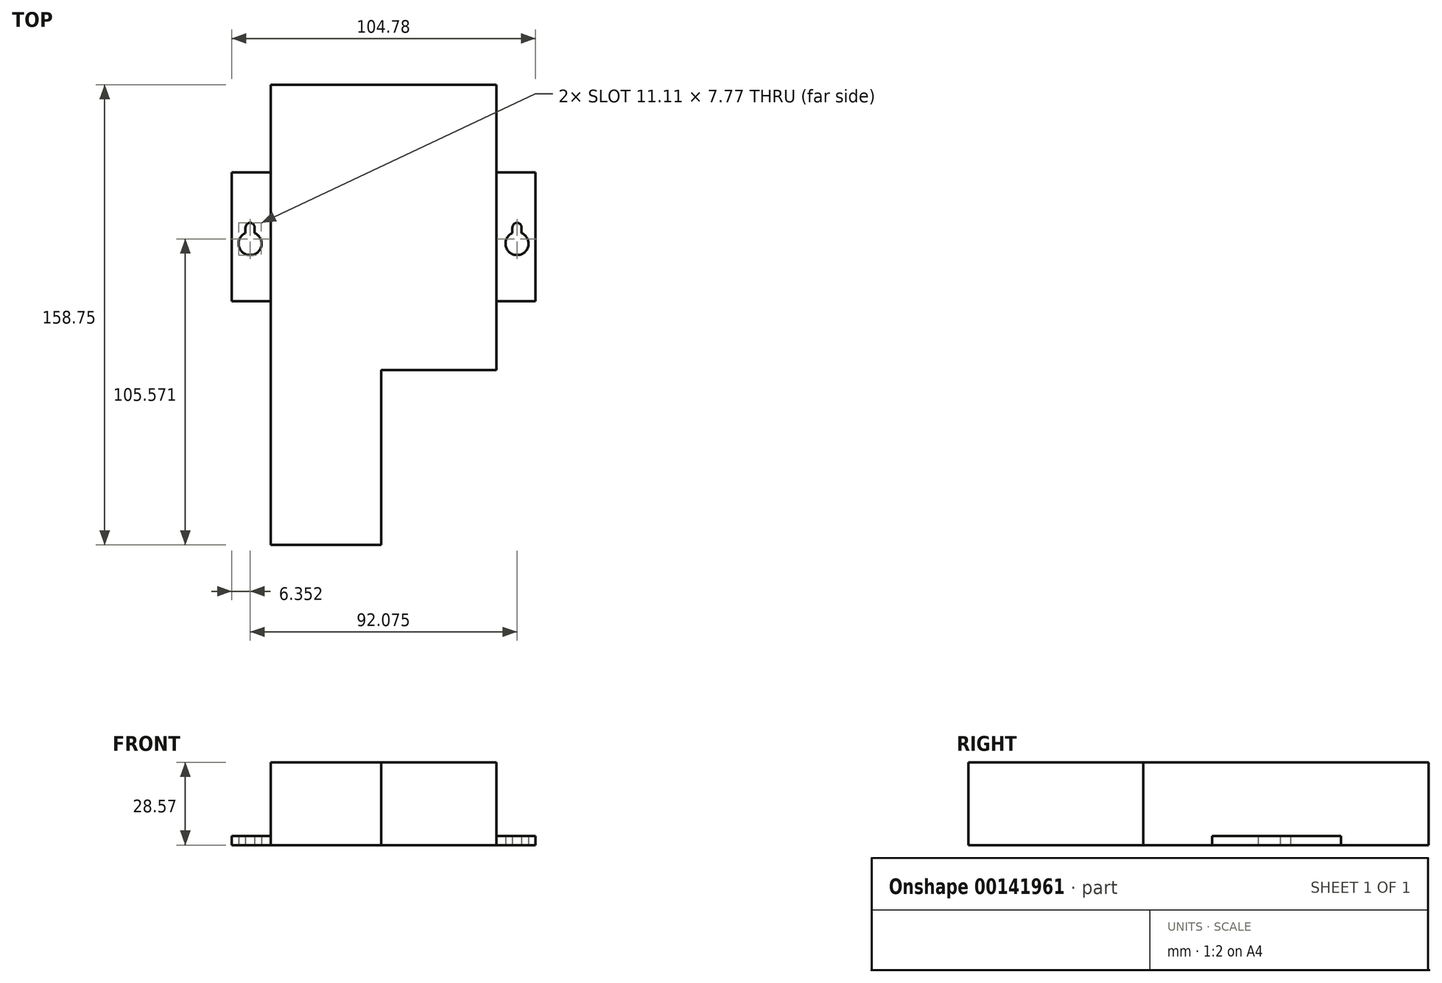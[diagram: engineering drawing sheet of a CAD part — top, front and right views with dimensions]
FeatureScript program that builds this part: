
annotation { "Feature Type Name" : "Feature", "Feature Type Description" : "" }
export const myFeature = defineFeature(function(context is Context, id is Id, definition is map)
    precondition{}
    {
        {
            var Q0;
            Q0=qCreatedBy(makeId("Top.planeOp"),FACE);
            var sketch = newSketch(context, id + "F0", { "sketchPlane" : qUnion([Q0])});
            skLineSegment(sketch, "E0.bottom", {"start": v(-38.9, -49.21) * mm, "end": v(38.9, -49.21) * mm});
            skLineSegment(sketch, "E0.top", {"start": v(-38.9, 49.21) * mm, "end": v(38.9, 49.21) * mm});
            skLineSegment(sketch, "E0.left", {"start": v(-38.9, -49.21) * mm, "end": v(-38.9, 49.21) * mm});
            skLineSegment(sketch, "E0.right", {"start": v(38.9, -49.21) * mm, "end": v(38.9, 49.21) * mm});
            skPoint(sketch, "E0.middle", {"position": v(0, 0) * mm});
            skSolve(sketch);
        }
        {
            var Q0;
            Q0 = qSketchRegion(id + "F0", true);
            extrude(context, id + "F1", {"entities" : qUnion([Q0]), "depth" : 28.57 * mm});
        }
        {
            var Q0;
            Q0=makeQuery(id+"F1.opExtrude","CAP_FACE",FACE,{"disambiguationData":[OSD([sQuery(id+"F0.wireOp",EDGE,"E0.bottom"),sQuery(id+"F0.wireOp",EDGE,"E0.top"),sQuery(id+"F0.wireOp",EDGE,"E0.left"),sQuery(id+"F0.wireOp",EDGE,"E0.right")])],"isStart":true});
            var sketch = newSketch(context, id + "F2", { "sketchPlane" : qUnion([Q0])});
            skPoint(sketch, "E1.middle", {"position": v(0, 0) * mm});
            skCircle(sketch, "E2", {"center": v(-46.04, 5.56) * mm, "radius": 3.97 * mm});
            skLineSegment(sketch, "E3", {"start": v(-46.04, 5.56) * mm, "end": v(-46.04, 0) * mm, "construction": true});
            skArc(sketch, "E4.0.startCap", {"start": v(-47.63, 5.56) * mm, "mid": v(-46.04, 7.14) * mm, "end": v(-44.45, 5.56) * mm});
            skArc(sketch, "E4.0.endCap", {"start": v(-44.45, 0) * mm, "mid": v(-46.04, -1.59) * mm, "end": v(-47.63, 0) * mm});
            skLineSegment(sketch, "E4.0.left", {"start": v(-44.45, 5.56) * mm, "end": v(-44.45, 0) * mm});
            skLineSegment(sketch, "E4.0.right", {"start": v(-47.63, 5.56) * mm, "end": v(-47.63, 0) * mm});
            skLineSegment(sketch, "E5", {"start": v(0, 0) * mm, "end": v(0, -42.43) * mm, "construction": true});
            skLineSegment(sketch, "E6.MirrorCS", {"start": v(46.04, 5.56) * mm, "end": v(46.04, 0) * mm, "construction": true});
            skCircle(sketch, "E7.MirrorC", {"center": v(46.04, 5.56) * mm, "radius": 3.97 * mm});
            skArc(sketch, "E8.MirrorCS", {"start": v(47.63, 5.56) * mm, "mid": v(46.04, 7.14) * mm, "end": v(44.45, 5.56) * mm});
            skArc(sketch, "E9.MirrorCS", {"start": v(44.45, 0) * mm, "mid": v(46.04, -1.59) * mm, "end": v(47.63, 0) * mm});
            skLineSegment(sketch, "E10.MirrorCS", {"start": v(44.45, 5.56) * mm, "end": v(44.45, 0) * mm});
            skLineSegment(sketch, "E11.MirrorCS", {"start": v(47.62, 5.56) * mm, "end": v(47.62, 0) * mm});
            skLineSegment(sketch, "E12.bottom", {"start": v(-52.39, 25.4) * mm, "end": v(52.39, 25.4) * mm});
            skLineSegment(sketch, "E12.top", {"start": v(-52.39, -19.05) * mm, "end": v(52.39, -19.05) * mm});
            skLineSegment(sketch, "E12.left", {"start": v(-52.39, 25.4) * mm, "end": v(-52.39, -19.05) * mm});
            skLineSegment(sketch, "E12.right", {"start": v(52.39, 25.4) * mm, "end": v(52.39, -19.05) * mm});
            skLineSegment(sketch, "E13", {"start": v(0, 49.21) * mm, "end": v(0, 25.4) * mm, "construction": true});
            skSolve(sketch);
        }
        {
            var Q0;
            Q0 = qSketchRegion(id + "F2", true);
            extrude(context, id + "F3", {"entities" : qUnion([Q0]), "operationType" : NewBodyOperationType.ADD, "oppositeDirection" : true, "depth" : 3.17 * mm});
        }
        {
            var Q0;
            Q0=makeQuery(id+"F1.opExtrude","SWEPT_FACE",FACE,{"disambiguationData":[OSD([sQuery(id+"F0.wireOp",EDGE,"E0.bottom")])]});
            var sketch = newSketch(context, id + "F4", { "sketchPlane" : qUnion([Q0])});
            skLineSegment(sketch, "E14.bottom", {"start": v(-38.9, 0) * mm, "end": v(-0.8, 0) * mm});
            skLineSegment(sketch, "E14.top", {"start": v(-38.9, 28.58) * mm, "end": v(-0.8, 28.58) * mm});
            skLineSegment(sketch, "E14.left", {"start": v(-38.9, 0) * mm, "end": v(-38.9, 28.58) * mm});
            skLineSegment(sketch, "E14.right", {"start": v(-0.8, 0) * mm, "end": v(-0.8, 28.58) * mm});
            skSolve(sketch);
        }
        {
            var Q0;
            Q0 = qSketchRegion(id + "F4", true);
            extrude(context, id + "F5", {"entities" : qUnion([Q0]), "operationType" : NewBodyOperationType.ADD, "depth" : 60.32 * mm});
        }
    });
